# Revit family: Grohe_PlumbingFixture_Essence_SingleLeverMixer_235900011
name_source: partatom
category: Plumbing Fixtures
revit_build: Autodesk Revit 2018 (Build: 20190510_1515(x64)
units: mm (PartAtom-declared; Revit-internal decimal feet)

## family parameters
Cut with Voids When Loaded = No
Host = Face
OmniClass Number = 23.45.55.17
OmniClass Title = Mixing Faucets
Part Type = Normal
Room Calculation Point = No
Round Connector Dimension = Use Diameter
Shared = No

## types (1)
- 23590001
    ADACompliant = No
    Assembly Code = D2010
    AssetType = Fixed
    BIMObjectName = Grohe_PlumbingFixture_Essence_SingleLeverMixer_23590001
    CWFU = 4.5
    ClassificationName = Uniclass 2015
    ClassificationValue = Pr_40_20_87_98
    ColdWaterConnectionDiameter = 10 mm  [stored 0.0328084 ft]
    Cost = 0 $
    Default Elevation = 0 mm  [stored 0 ft]
    Description = • monobloc installation • metal lever • 28 mm ceramic cartridge with GROHE SilkMove • with temperature limiter • GROHE StarLight chrome finish GROHE EcoJoy mousseur 5.7 l/min GROHE AquaGuide adjustable mousseur GROHE QuickFix Plus installation system smooth body flexible connection hoses
    DocumentationCertificates = www.bimstore.co
    DocumentationInstallationGuide = www.bimstore.co
    DocumentationLiterature = www.bimstore.co
    DocumentationMaintenance = www.bimstore.co
    DocumentationTechnical = www.bimstore.co
    DurationUnit = Years
    Ecojoy = Yes
    ExpectedLife = 0
    FaucetMaterial = Grohe-Chrome
    Features = GROHE Blue Mono mixer with filter function monobloc installation C-spout touch operated for 3 types of filtered and chilled water still, medium, sparkling GROHE StarLight chrome finish swivel tubular spout swivel area 150° GROHE Blue Professional cooler delivers 12 liters of chilled sparkling water per hour colour display with push and turn control 270 Watt cooling unit, 230 V, 50 Hz type of protection IP 21 CE approved requires ventilation holes in the bottom of the kitchen cabinet software set-up and monitoring of filter and CO2 capacity possible via GROHE Ondus app push notifications at low filter resp. CO2 capacity additional monitoring via GROHE Blue Professional Browser-Monitor possible with Bluetooth 4.0* and WIFI interface for wireless data communication for Apple** and Android devices Bluetooth range (max. 10 m) varies depending on materials used and walls between transmitter and receiver filter head with flexible water hardness adjustment GROHE Blue filter, CO2 bottle and cleaning cartridge are not included in the delivery and have to be ordered separately suitable filters: - filter S-size, capacity 600 l at 20° dKH (40 404 001) - filter M-size, capacity 1500 l at 20° dKH (40 430 001) - filter L-size, capacity 2500 l at 20° dKH (40 412 001) - acctivated carbon filter, capacity 3000 l (40 547 001 - Magnesium+ filter, capacity 400 l at 17° dGH (40 691 001)System requirements Apple iPhone with iOS 9.0 or higher System requirements Android smart phone with Android 4.3 or higher Mobile devices and GROHE Ondus App*** are not included in delivery and have to be ordered separately via an authorised Apple store/store/iTunes or Google Play store. The Bluetooth word mark and logos are registered trademarks owned by Bluetooth SIG, Inc. and any use of such marks by Grohe AG is under
    Finish = Stainless Steel
    HWFU = 4.5
    HotWaterConnectionDiameter = 10 mm  [stored 0.0328084 ft]
    IfcExportAs = IfcPipeFitting
    IfcExportType = IfcPipeFittingType
    Keynote = N13
    LowEmittingMaterial = No
    Manufacturer = Grohe
    ManufacturerName = Grohe
    MasterformatNumber = 01 52 19
    MasterformatTitle = Sanitary Facilities
    Material = Chrome
    Model = Essence Single-lever basin mixer 1/2" S-Size
    ModelNumber = 23590001
    ModelReference = Essence Single-lever basin mixer 1/2" S-Size
    NBSDescription = Washbasin taps
    NBSObjectName = Grohe - Water supply fittings for wash basins and troughs
    NBSReference = 45-35-70/371
    NominalDepth = 0 mm  [stored 0 ft]
    NominalHeight = 0 mm  [stored 0 ft]
    NominalLength = 0 mm  [stored 0 ft]
    PipeMaterial = GroheLimited-Pipework
    ProductDocumentationLink = https://cdn.cloud.grohe.com
    ProductPageURL = https://www.grohe.co.uk
    ProductionYear = 2020
    Type Comments = 23590001
    TypeName = 23590001
    URL = www.grohe.com
    WarrantyDurationLabor = 0
    WarrantyDurationParts = 0
    WarrantyDurationUnit = Years
    _BSBibleVersion = 16
    _BimSpecGuid = 0
    _CurrentRevision = 1
    _DistributedBy = www.bimstore.co
    _ObjectUserGuide = www.bimstore.co

note: [stored X ft] marks values corroborated as IEEE doubles in the binary element streams (Revit-internal decimal feet)

## geometry (parser evidence)
native form markers: Sweep x2
no freeform markers — native parametric forms only
